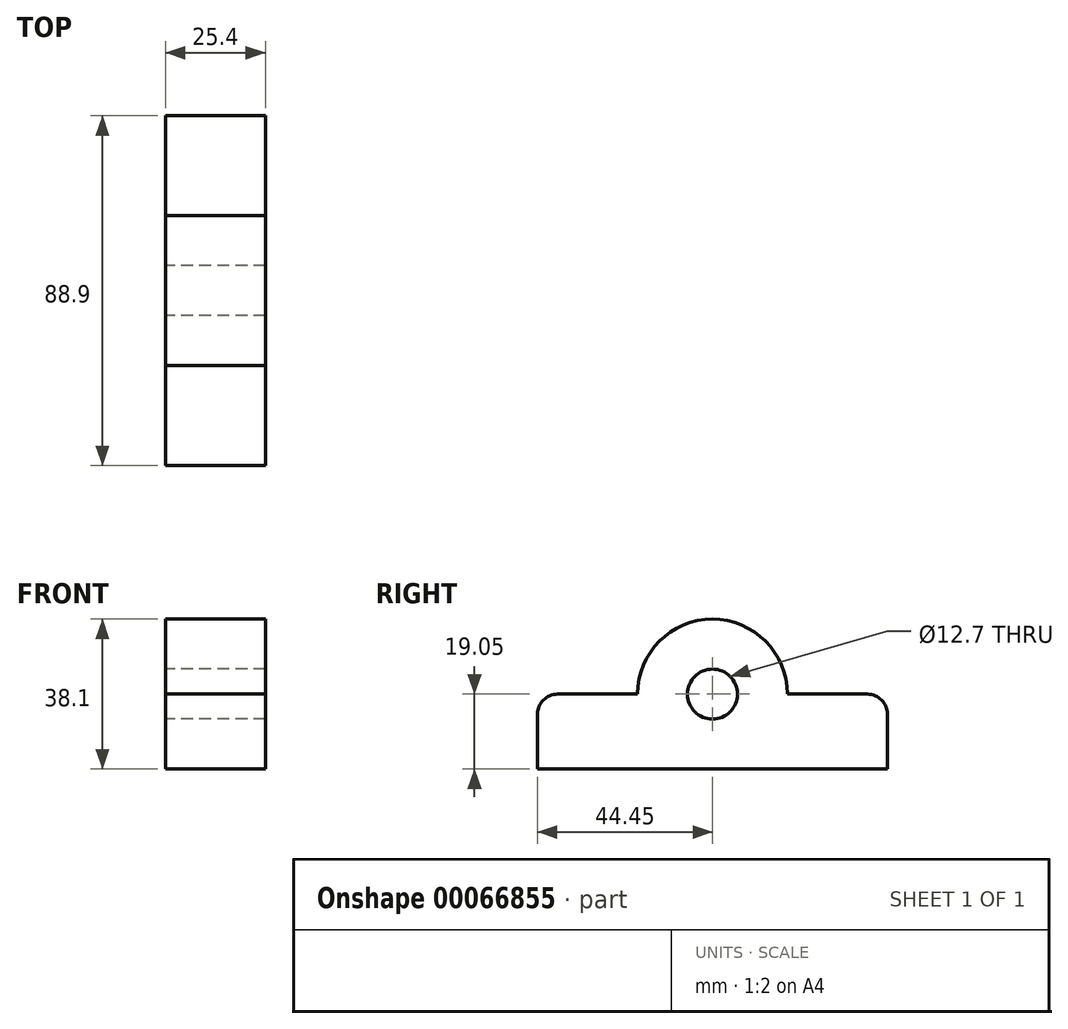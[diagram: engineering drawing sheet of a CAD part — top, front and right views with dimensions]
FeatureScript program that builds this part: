
annotation { "Feature Type Name" : "Feature", "Feature Type Description" : "" }
export const myFeature = defineFeature(function(context is Context, id is Id, definition is map)
    precondition{}
    {
        {
            var Q0;
            Q0=qCreatedBy(makeId("Right.planeOp"),FACE);
            var sketch = newSketch(context, id + "F0", { "sketchPlane" : qUnion([Q0])});
            skArc(sketch, "E0", {"start": v(19.05, 0) * mm, "mid": v(0, 19.05) * mm, "end": v(-19.05, 0) * mm});
            skLineSegment(sketch, "E1.bottom", {"start": v(-44.45, 0) * mm, "end": v(-19.05, 0) * mm});
            skLineSegment(sketch, "E1.top", {"start": v(-44.45, -19.05) * mm, "end": v(44.45, -19.05) * mm});
            skLineSegment(sketch, "E1.left", {"start": v(-44.45, 0) * mm, "end": v(-44.45, -19.05) * mm});
            skLineSegment(sketch, "E1.right", {"start": v(44.45, 0) * mm, "end": v(44.45, -19.05) * mm});
            skLineSegment(sketch, "E2.trimOffspring", {"start": v(19.05, 0) * mm, "end": v(44.45, 0) * mm});
            skCircle(sketch, "E3", {"center": v(0, 0) * mm, "radius": 6.35 * mm});
            skSolve(sketch);
        }
        {
            var Q0;
            Q0=makeQuery(id+"F0.imprint","IMPRINT",FACE,{"disambiguationData":[TD([[makeQuery(id+"F0.imprint","IMPRINT",EDGE,{"derivedFrom":sQuery(id+"F0.wireOp",EDGE,"E0")}),1.0]])]});
            extrude(context, id + "F1", {"entities" : qUnion([Q0]), "depth" : 25.4 * mm});
        }
        {
            var Q0;
            Q0=makeQuery(id+"F1.opExtrude","SWEPT_EDGE",EDGE,{"disambiguationData":[OSD([sQuery(id+"F0.wireOp",EDGE,"E1.right"),sQuery(id+"F0.wireOp",EDGE,"E2.trimOffspring")])]});
            fillet(context, id + "F2", {"entities" : qUnion([Q0]), "radius" : 5.08 * mm, "tangentPropagation" : true, "allowEdgeOverflow" : false});
        }
        {
            var Q0;
            Q0=makeQuery(id+"F1.opExtrude","SWEPT_EDGE",EDGE,{"disambiguationData":[OSD([sQuery(id+"F0.wireOp",EDGE,"E1.bottom"),sQuery(id+"F0.wireOp",EDGE,"E1.left")])]});
            fillet(context, id + "F3", {"entities" : qUnion([Q0]), "radius" : 5.08 * mm, "tangentPropagation" : true, "allowEdgeOverflow" : false});
        }
    });
